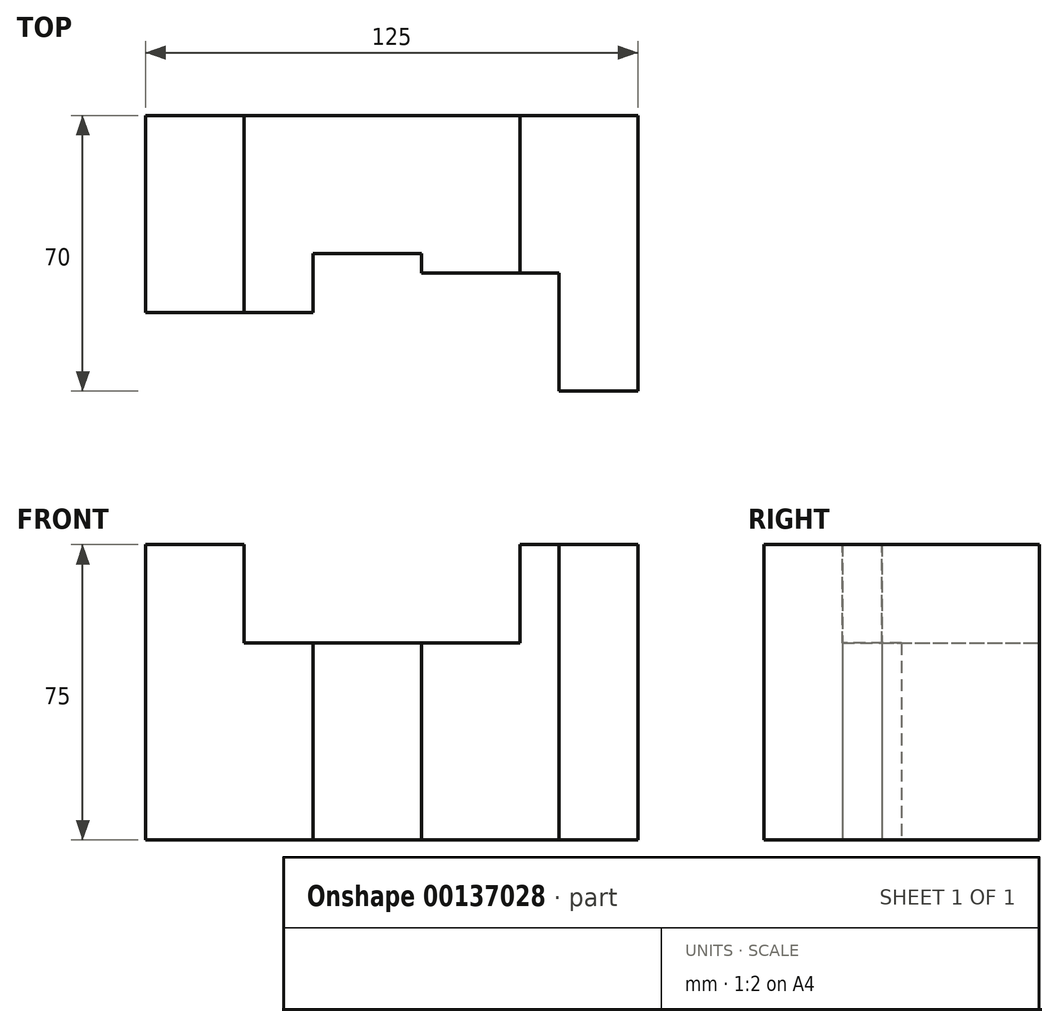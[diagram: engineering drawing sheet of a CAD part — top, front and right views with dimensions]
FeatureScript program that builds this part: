
annotation { "Feature Type Name" : "Feature", "Feature Type Description" : "" }
export const myFeature = defineFeature(function(context is Context, id is Id, definition is map)
    precondition{}
    {
        {
            var Q0;
            Q0=qCreatedBy(makeId("Top.planeOp"),FACE);
            var sketch = newSketch(context, id + "F0", { "sketchPlane" : qUnion([Q0])});
            skLineSegment(sketch, "E0.bottom", {"start": v(0, 0) * mm, "end": v(125, 0) * mm, "construction": true});
            skLineSegment(sketch, "E0.top", {"start": v(0, 70) * mm, "end": v(125, 70) * mm, "construction": true});
            skLineSegment(sketch, "E0.left", {"start": v(0, 0) * mm, "end": v(0, 70) * mm, "construction": true});
            skLineSegment(sketch, "E0.right", {"start": v(125, 0) * mm, "end": v(125, 70) * mm, "construction": true});
            skLineSegment(sketch, "E1", {"start": v(125, 70) * mm, "end": v(125, 0) * mm});
            skLineSegment(sketch, "E2", {"start": v(125, 0) * mm, "end": v(105, 0) * mm});
            skLineSegment(sketch, "E3", {"start": v(105, 0) * mm, "end": v(105, 30) * mm});
            skLineSegment(sketch, "E4", {"start": v(105, 30) * mm, "end": v(70, 30) * mm});
            skLineSegment(sketch, "E5", {"start": v(70, 30) * mm, "end": v(70, 35) * mm});
            skLineSegment(sketch, "E6", {"start": v(70, 35) * mm, "end": v(42.5, 35) * mm});
            skLineSegment(sketch, "E7", {"start": v(42.5, 35) * mm, "end": v(42.5, 20) * mm});
            skLineSegment(sketch, "E8", {"start": v(42.5, 20) * mm, "end": v(0, 20) * mm});
            skLineSegment(sketch, "E9", {"start": v(0, 20) * mm, "end": v(0, 70) * mm});
            skLineSegment(sketch, "E10", {"start": v(0, 70) * mm, "end": v(125, 70) * mm});
            skSolve(sketch);
        }
        {
            var Q0;
            Q0=makeQuery(id+"F0.imprint","IMPRINT",FACE,{"disambiguationData":[TD([[makeQuery(id+"F0.imprint","IMPRINT",EDGE,{"derivedFrom":sQuery(id+"F0.wireOp",EDGE,"E1")}),-1.0]])]});
            extrude(context, id + "F1", {"entities" : qUnion([Q0]), "depth" : 75 * mm});
        }
        {
            var Q0;
            Q0=makeQuery(id+"F1.opExtrude","SWEPT_FACE",FACE,{"disambiguationData":[OSD([sQuery(id+"F0.wireOp",EDGE,"E10")])]});
            var sketch = newSketch(context, id + "F2", { "sketchPlane" : qUnion([Q0])});
            skLineSegment(sketch, "E11.bottom", {"start": v(-125, 75) * mm, "end": v(0, 75) * mm, "construction": true});
            skLineSegment(sketch, "E11.top", {"start": v(-125, 50) * mm, "end": v(0, 50) * mm, "construction": true});
            skLineSegment(sketch, "E11.left", {"start": v(-125, 75) * mm, "end": v(-125, 50) * mm, "construction": true});
            skLineSegment(sketch, "E11.right", {"start": v(0, 75) * mm, "end": v(0, 50) * mm, "construction": true});
            skLineSegment(sketch, "E12.bottom", {"start": v(-25, 75) * mm, "end": v(-95, 75) * mm});
            skLineSegment(sketch, "E12.top", {"start": v(-25, 50) * mm, "end": v(-95, 50) * mm});
            skLineSegment(sketch, "E12.left", {"start": v(-25, 75) * mm, "end": v(-25, 50) * mm});
            skLineSegment(sketch, "E12.right", {"start": v(-95, 75) * mm, "end": v(-95, 50) * mm});
            skSolve(sketch);
        }
        {
            var Q0;
            Q0=makeQuery(id+"F2.imprint","IMPRINT",FACE,{"disambiguationData":[TD([[makeQuery(id+"F2.imprint","IMPRINT",EDGE,{"derivedFrom":sQuery(id+"F2.wireOp",EDGE,"E12.bottom")}),1.0]])]});
            extrude(context, id + "F3", {"entities" : qUnion([Q0]), "operationType" : NewBodyOperationType.REMOVE, "endBound" : BoundingType.THROUGH_ALL, "oppositeDirection" : true, "depth" : 25 * mm});
        }
    });
